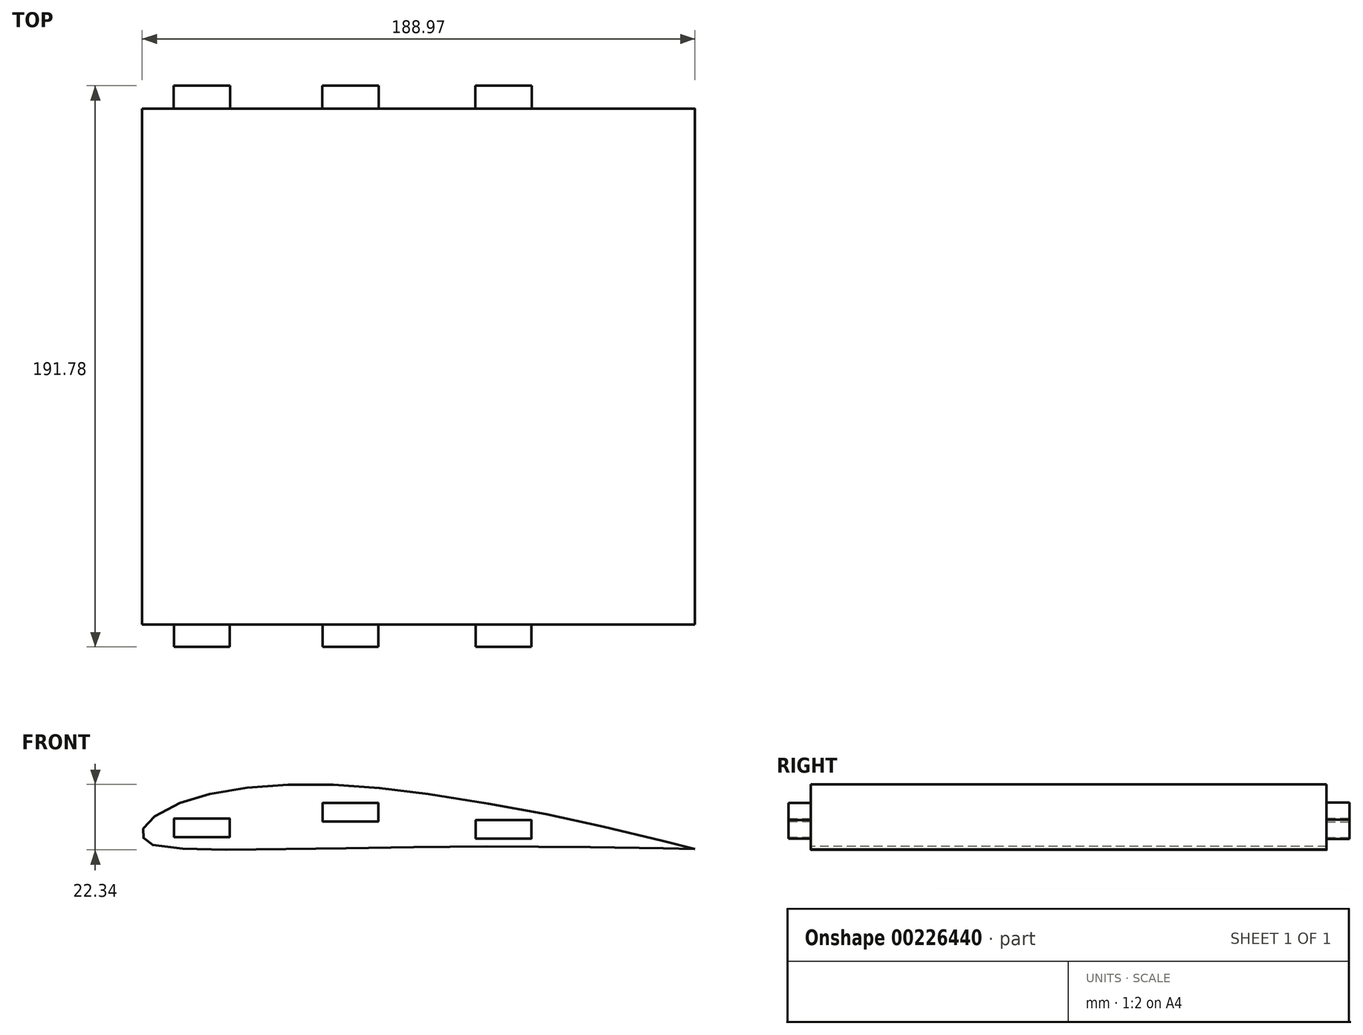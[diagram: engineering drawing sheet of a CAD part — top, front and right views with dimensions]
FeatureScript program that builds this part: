
annotation { "Feature Type Name" : "Feature", "Feature Type Description" : "" }
export const myFeature = defineFeature(function(context is Context, id is Id, definition is map)
    precondition{}
    {
        {
            var Q0;
            Q0=qCreatedBy(makeId("Front.planeOp"),FACE);
            var sketch = newSketch(context, id + "F0", { "sketchPlane" : qUnion([Q0])});
            skFitSpline(sketch, "E0.0", {"points": [v(330.51, -26.8) * mm, v(330.41, -27.02) * mm, v(320.9, -26.65) * mm, v(282.9, -25.74) * mm, v(133.46, -23.45) * mm, v(-1.4, -24.3) * mm, v(-5.52, -24.35) * mm, v(-223.27, -27.63) * mm, v(-263.84, -26.15) * mm, v(-289.63, -25.37) * mm, v(-306.1, -22.64) * mm, v(-310.34, -21.37) * mm, v(-312.97, -20.17) * mm, v(-315.36, -18.5) * mm, v(-317.44, -16.46) * mm, v(-318.92, -14.43) * mm, v(-319.94, -12.57) * mm, v(-320.57, -10.76) * mm, v(-320.82, -9.61) * mm, v(-320.99, -7.97) * mm, v(-320.86, -6.28) * mm, v(-320.4, -4.3) * mm, v(-319.53, -2.04) * mm, v(-317.5, 1.34) * mm, v(-314.64, 4.78) * mm, v(-309.38, 9.62) * mm, v(-300.92, 15.27) * mm, v(-284.86, 23.88) * mm, v(-268.85, 30.71) * mm, v(-251.3, 35.74) * mm, v(-225.1, 41.46) * mm, v(-196.52, 45.77) * mm, v(-164.68, 48.46) * mm, v(-128.36, 49.34) * mm, v(-84.95, 48.6) * mm, v(-42.8, 45.45) * mm, v(0.59, 40.3) * mm, v(69.38, 29.76) * mm, v(139.47, 17.63) * mm, v(201.78, 4.38) * mm, v(277.63, -13.26) * mm, v(320.71, -24.55) * mm, v(330.61, -26.58) * mm, v(330.51, -26.8) * mm]});
            skPoint(sketch, "E1", {"position": v(330.51, -26.8) * mm});
            skPoint(sketch, "E2", {"position": v(-320.85, -9.19) * mm});
            skSolve(sketch);
        }
        {
            var Q0;
            Q0=makeQuery(id+"F0.imprint","IMPRINT",FACE,{"disambiguationData":[TD([[makeQuery(id+"F0.imprint","IMPRINT",EDGE,{"derivedFrom":sQuery(id+"F0.wireOp",EDGE,"E0.0")}),-1.0]])]});
            extrude(context, id + "F1", {"entities" : qUnion([Q0]), "depth" : 635 * mm, "symmetric" : true});
        }
        {
            var Q0;
            Q0=makeQuery(id+"F1.opExtrude","SWEPT_BODY",BODY,{"disambiguationData":[OSD([sQuery(id+"F0.wireOp",EDGE,"E0.0")])]});
            var Q1;
            Q1=qCreatedBy(makeId("Origin.pointOp"),VERTEX);
            transform(context, id + "F2", {"entities" : qUnion([Q0]), "transformType" : TransformType.SCALE_UNIFORMLY, "scale" : .29, "scalePoint" : qUnion([Q1]), "makeCopy" : false});
        }
        {
            var Q0;
            Q0=makeQuery(id+"F1.opExtrude","CAP_FACE",FACE,{"disambiguationData":[OSD([sQuery(id+"F0.wireOp",EDGE,"E0.0")])],"isStart":false});
            var sketch = newSketch(context, id + "F3", { "sketchPlane" : qUnion([Q0])});
            skFitSpline(sketch, "E3.0", {"points": [v(95.85, -7.77) * mm, v(95.82, -7.84) * mm, v(93.06, -7.73) * mm, v(82.04, -7.47) * mm, v(38.7, -6.8) * mm, v(-0.4, -7.05) * mm, v(-1.6, -7.06) * mm, v(-64.75, -8.01) * mm, v(-76.51, -7.58) * mm, v(-84, -7.36) * mm, v(-88.77, -6.57) * mm, v(-90, -6.2) * mm, v(-90.76, -5.85) * mm, v(-91.45, -5.37) * mm, v(-92.06, -4.77) * mm, v(-92.49, -4.19) * mm, v(-92.78, -3.65) * mm, v(-92.96, -3.12) * mm, v(-93.04, -2.79) * mm, v(-93.09, -2.31) * mm, v(-93.05, -1.82) * mm, v(-92.92, -1.25) * mm, v(-92.66, -0.6) * mm, v(-92.08, 0.39) * mm, v(-91.24, 1.39) * mm, v(-89.72, 2.79) * mm, v(-87.27, 4.43) * mm, v(-82.61, 6.93) * mm, v(-77.97, 8.9) * mm, v(-72.88, 10.37) * mm, v(-65.28, 12.02) * mm, v(-57, 13.27) * mm, v(-47.76, 14.05) * mm, v(-37.23, 14.3) * mm, v(-24.64, 14.1) * mm, v(-12.41, 13.18) * mm, v(0.17, 11.69) * mm, v(20.12, 8.63) * mm, v(40.45, 5.11) * mm, v(58.52, 1.27) * mm, v(80.51, -3.84) * mm, v(93, -7.12) * mm, v(95.88, -7.7) * mm, v(95.85, -7.77) * mm]});
            skPoint(sketch, "E4", {"position": v(-93.07, -2.2) * mm});
            skPoint(sketch, "E5", {"position": v(95.64, -7.8) * mm});
            skLineSegment(sketch, "E6.bottom", {"start": v(-63.23, -3.61) * mm, "end": v(-82.28, -3.61) * mm});
            skLineSegment(sketch, "E6.top", {"start": v(-63.23, 2.74) * mm, "end": v(-82.28, 2.74) * mm});
            skLineSegment(sketch, "E6.left", {"start": v(-63.23, -3.61) * mm, "end": v(-63.23, 2.74) * mm});
            skLineSegment(sketch, "E6.right", {"start": v(-82.28, -3.61) * mm, "end": v(-82.28, 2.74) * mm});
            skPoint(sketch, "E6.middle", {"position": v(-72.75, -0.44) * mm});
            skLineSegment(sketch, "E7.bottom", {"start": v(-12.43, 1.72) * mm, "end": v(-31.48, 1.72) * mm});
            skLineSegment(sketch, "E7.top", {"start": v(-12.43, 8.07) * mm, "end": v(-31.48, 8.07) * mm});
            skLineSegment(sketch, "E7.left", {"start": v(-12.43, 1.72) * mm, "end": v(-12.43, 8.07) * mm});
            skLineSegment(sketch, "E7.right", {"start": v(-31.48, 1.72) * mm, "end": v(-31.48, 8.07) * mm});
            skPoint(sketch, "E7.middle", {"position": v(-21.95, 4.9) * mm});
            skLineSegment(sketch, "E8.bottom", {"start": v(40, -4.2) * mm, "end": v(20.95, -4.2) * mm});
            skLineSegment(sketch, "E8.top", {"start": v(40, 2.16) * mm, "end": v(20.95, 2.16) * mm});
            skLineSegment(sketch, "E8.left", {"start": v(40, -4.2) * mm, "end": v(40, 2.16) * mm});
            skLineSegment(sketch, "E8.right", {"start": v(20.95, -4.2) * mm, "end": v(20.95, 2.16) * mm});
            skPoint(sketch, "E8.middle", {"position": v(30.48, -1.02) * mm});
            skLineSegment(sketch, "E9", {"start": v(95.64, -7.8) * mm, "end": v(-115.1, -7.8) * mm, "construction": true});
            skSolve(sketch);
        }
        {
            var Q0;
            Q0=makeQuery(id+"F3.imprint","IMPRINT",FACE,{"disambiguationData":[TD([[makeQuery(id+"F3.imprint","IMPRINT",EDGE,{"derivedFrom":sQuery(id+"F3.wireOp",EDGE,"E6.bottom")}),-1.0]])]});
            var Q1;
            Q1=makeQuery(id+"F3.imprint","IMPRINT",FACE,{"disambiguationData":[TD([[makeQuery(id+"F3.imprint","IMPRINT",EDGE,{"derivedFrom":sQuery(id+"F3.wireOp",EDGE,"E7.bottom")}),-1.0]])]});
            var Q2;
            Q2=makeQuery(id+"F3.imprint","IMPRINT",FACE,{"disambiguationData":[TD([[makeQuery(id+"F3.imprint","IMPRINT",EDGE,{"derivedFrom":sQuery(id+"F3.wireOp",EDGE,"E8.bottom")}),-1.0]])]});
            extrude(context, id + "F4", {"entities" : qUnion([Q0, Q1, Q2]), "operationType" : NewBodyOperationType.ADD, "depth" : 7.62 * mm});
        }
        {
            var Q0;
            Q0=makeQuery(id+"F1.opExtrude","CAP_FACE",FACE,{"disambiguationData":[OSD([sQuery(id+"F0.wireOp",EDGE,"E0.0")])],"isStart":true});
            var sketch = newSketch(context, id + "F5", { "sketchPlane" : qUnion([Q0])});
            skPoint(sketch, "E10.0", {"position": v(-30.48, -1.02) * mm});
            skPoint(sketch, "E10.1", {"position": v(21.95, 4.9) * mm});
            skPoint(sketch, "E10.2", {"position": v(72.75, -0.44) * mm});
            skLineSegment(sketch, "E11.bottom", {"start": v(-20.83, 2.29) * mm, "end": v(-40.13, 2.29) * mm});
            skLineSegment(sketch, "E11.top", {"start": v(-20.83, -4.32) * mm, "end": v(-40.13, -4.32) * mm});
            skLineSegment(sketch, "E11.left", {"start": v(-20.83, 2.29) * mm, "end": v(-20.83, -4.32) * mm});
            skLineSegment(sketch, "E11.right", {"start": v(-40.13, 2.29) * mm, "end": v(-40.13, -4.32) * mm});
            skLineSegment(sketch, "E12.bottom", {"start": v(31.6, 1.6) * mm, "end": v(12.3, 1.6) * mm});
            skLineSegment(sketch, "E12.top", {"start": v(31.6, 8.2) * mm, "end": v(12.3, 8.2) * mm});
            skLineSegment(sketch, "E12.left", {"start": v(31.6, 1.6) * mm, "end": v(31.6, 8.2) * mm});
            skLineSegment(sketch, "E12.right", {"start": v(12.3, 1.6) * mm, "end": v(12.3, 8.2) * mm});
            skLineSegment(sketch, "E13.bottom", {"start": v(63.1, 2.86) * mm, "end": v(82.4, 2.86) * mm});
            skLineSegment(sketch, "E13.top", {"start": v(63.1, -3.74) * mm, "end": v(82.4, -3.74) * mm});
            skLineSegment(sketch, "E13.left", {"start": v(63.1, 2.86) * mm, "end": v(63.1, -3.74) * mm});
            skLineSegment(sketch, "E13.right", {"start": v(82.4, 2.86) * mm, "end": v(82.4, -3.74) * mm});
            skFitSpline(sketch, "E14.0", {"points": [v(-95.85, -7.77) * mm, v(-95.82, -7.84) * mm, v(-93.06, -7.73) * mm, v(-82.04, -7.47) * mm, v(-38.7, -6.8) * mm, v(0.4, -7.05) * mm, v(1.6, -7.06) * mm, v(64.75, -8.01) * mm, v(76.51, -7.58) * mm, v(84, -7.36) * mm, v(88.77, -6.57) * mm, v(90, -6.2) * mm, v(90.76, -5.85) * mm, v(91.45, -5.37) * mm, v(92.06, -4.77) * mm, v(92.49, -4.19) * mm, v(92.78, -3.65) * mm, v(92.96, -3.12) * mm, v(93.04, -2.79) * mm, v(93.09, -2.31) * mm, v(93.05, -1.82) * mm, v(92.92, -1.25) * mm, v(92.66, -0.6) * mm, v(92.08, 0.39) * mm, v(91.24, 1.39) * mm, v(89.72, 2.79) * mm, v(87.27, 4.43) * mm, v(82.61, 6.93) * mm, v(77.97, 8.9) * mm, v(72.88, 10.37) * mm, v(65.28, 12.02) * mm, v(57, 13.27) * mm, v(47.76, 14.05) * mm, v(37.23, 14.3) * mm, v(24.64, 14.1) * mm, v(12.41, 13.18) * mm, v(-0.17, 11.69) * mm, v(-20.12, 8.63) * mm, v(-40.45, 5.11) * mm, v(-58.52, 1.27) * mm, v(-80.51, -3.84) * mm, v(-93, -7.12) * mm, v(-95.88, -7.7) * mm, v(-95.85, -7.77) * mm]});
            skSolve(sketch);
        }
        {
            var Q0;
            Q0 = qSketchRegion(id + "F5", true);
            extrude(context, id + "F6", {"entities" : qUnion([Q0]), "operationType" : NewBodyOperationType.REMOVE, "oppositeDirection" : true, "depth" : 7.87 * mm});
        }
    });
